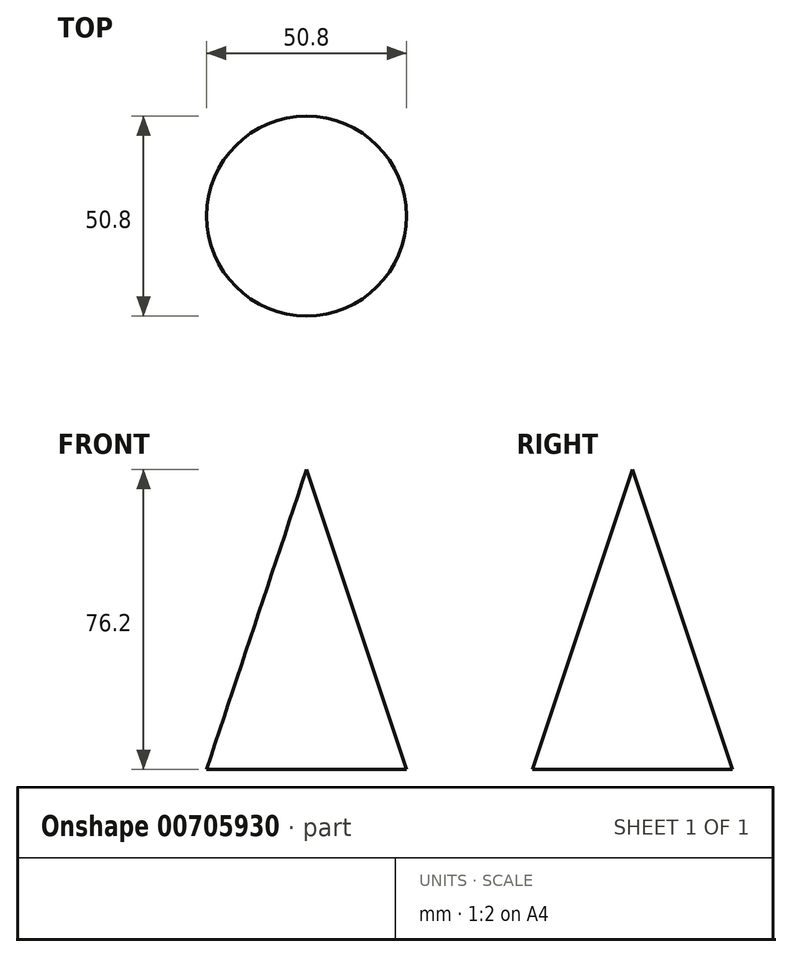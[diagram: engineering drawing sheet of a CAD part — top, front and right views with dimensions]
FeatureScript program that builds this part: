
annotation { "Feature Type Name" : "Feature", "Feature Type Description" : "" }
export const myFeature = defineFeature(function(context is Context, id is Id, definition is map)
    precondition{}
    {
        {
            var Q0;
            Q0=qCreatedBy(makeId("Front.planeOp"),FACE);
            var sketch = newSketch(context, id + "F0", { "sketchPlane" : qUnion([Q0])});
            skLineSegment(sketch, "E0.bottom", {"start": v(0, 0) * mm, "end": v(-25.4, 0) * mm});
            skLineSegment(sketch, "E0.left", {"start": v(0, 0) * mm, "end": v(0, 76.2) * mm});
            skLineSegment(sketch, "E1", {"start": v(-25.4, 0) * mm, "end": v(0, 76.2) * mm});
            skSolve(sketch);
        }
        {
            var Q0;
            Q0=makeQuery(id+"F0.imprint","IMPRINT",FACE,{"disambiguationData":[TD([[makeQuery(id+"F0.imprint","IMPRINT",EDGE,{"derivedFrom":sQuery(id+"F0.wireOp",EDGE,"E0.bottom")}),-1.0]])]});
            var Q1;
            Q1=sQuery(id+"F0.wireOp",EDGE,"E0.left");
            revolve(context, id + "F1", {"surfaceOperationType" : NewSurfaceOperationType.NEW, "entities" : qUnion([Q0]), "axis" : qUnion([Q1]), "revolveType" : RevolveType.FULL});
        }
    });
